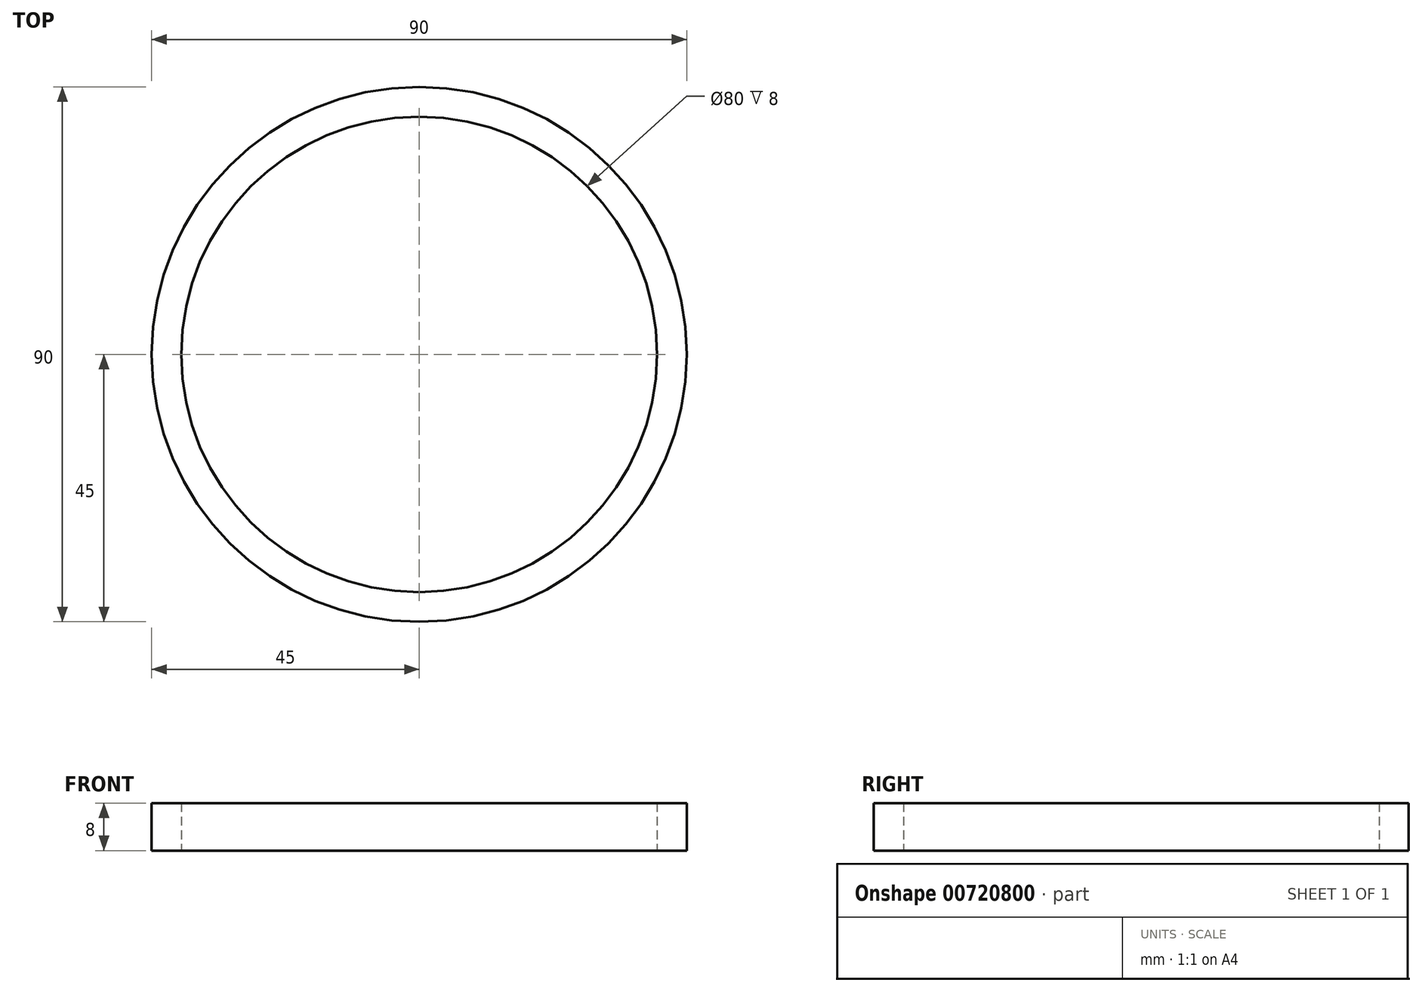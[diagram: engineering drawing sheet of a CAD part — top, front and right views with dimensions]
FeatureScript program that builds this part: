
annotation { "Feature Type Name" : "Feature", "Feature Type Description" : "" }
export const myFeature = defineFeature(function(context is Context, id is Id, definition is map)
    precondition{}
    {
        {
            var Q0;
            Q0=qCreatedBy(makeId("Top.planeOp"),FACE);
            var sketch = newSketch(context, id + "F0", { "sketchPlane" : qUnion([Q0])});
            skCircle(sketch, "E0", {"center": v(0, 0) * mm, "radius": 45 * mm});
            skSolve(sketch);
        }
        {
            var Q0;
            Q0 = qSketchRegion(id + "F0", true);
            extrude(context, id + "F1", {"entities" : qUnion([Q0]), "depth" : 8 * mm, "offsetDistance" : 25 * mm});
        }
        {
            var Q0;
            Q0=sQuery(id+"F0.wireOp",VERTEX,"E0.center");
            var Q1;
            Q1=makeQuery(id+"F1.opExtrude","SWEPT_BODY",BODY,{"disambiguationData":[OSD([sQuery(id+"F0.wireOp",EDGE,"E0")])]});
            hole(context, id + "F2", {"style" : HoleStyle.SIMPLE, "endStyle" : HoleEndStyle.BLIND, "oppositeDirection" : true, "holeDiameter" : 80 * mm, "majorDiameter" : 5 * mm, "holeDepth" : 60 * mm, "isTappedThrough" : true, "tappedDepth" : 12 * mm, "tapClearance" : 3, "locations" : qUnion([Q0]), "scope" : qUnion([Q1])});
        }
    });
